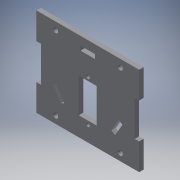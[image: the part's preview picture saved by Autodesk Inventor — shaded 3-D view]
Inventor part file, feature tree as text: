
AUTODESK INVENTOR PART (.ipt)
format: ipt  version: 2018 (Build 220112000, 112)  size: 155,136 bytes
history: native  units: in
note: dims shown in document units (in); Inventor stores cm internally (conversion verified against a paired STEP export)
features: reference x20, other x11, extrude x3, sketch x3
ambient origin geometry x8: Origin, YZ Plane, XZ Plane, XY Plane, X Axis, Y Axis, Z Axis, Center Point
bodies: Solid1 (feature_tree)
feature tree (37):
  extrude  "Extrusion1"  Depth=2.3622in
  extrude  "Extrusion2"  Depth=0.0039in
  extrude  "Extrusion3"  Depth=0.3937in
  sketch  "Sketch1"  dims[d0=2.7362in d1=2.3622in]
  reference  "Reference1"
  reference  "Reference2"
  reference  "Reference3"
  reference  "Reference4"
  sketch  "Sketch2"  dims[d2=0.0039in d3=0.0039in]
  reference  "Reference5"
  reference  "Reference6"
  reference  "Reference7"
  reference  "Reference8"
  sketch  "Sketch3"  dims[d4=0.0039in d5=0.0039in d6=0.4724in d7=0.4724in d8=0.1181in d9=0.1181in d10=0.0in d11=0.3056in d12=0.0in d13=0.002in d14=0.002in d15=0.002in d16=0.3937in d17=0.0in]
  reference  "Reference9"
  reference  "Reference10"
  reference  "Reference11"
  reference  "Reference12"
  reference  "Reference13"
  reference  "Reference14"
  reference  "Reference15"
  reference  "Reference16"
  reference  "Reference17"
  reference  "Reference18"
  reference  "Reference19"
  reference  "Reference20"
  other  "Camera pan and tilt assembly.iam"
  other  "Servo motor:3"
  other  "Servo body:1"
  other  "Angle bracket short:8"
  other  "Angle bracket short:6"
  other  "Angle bracket short:5"
  other  "Angle bracket short:7"
  other  "Bearing Support:3"
  other  "Bearing risers:1"
  other  "Bearing Support:2"
  other  "Bearing Support:1"
